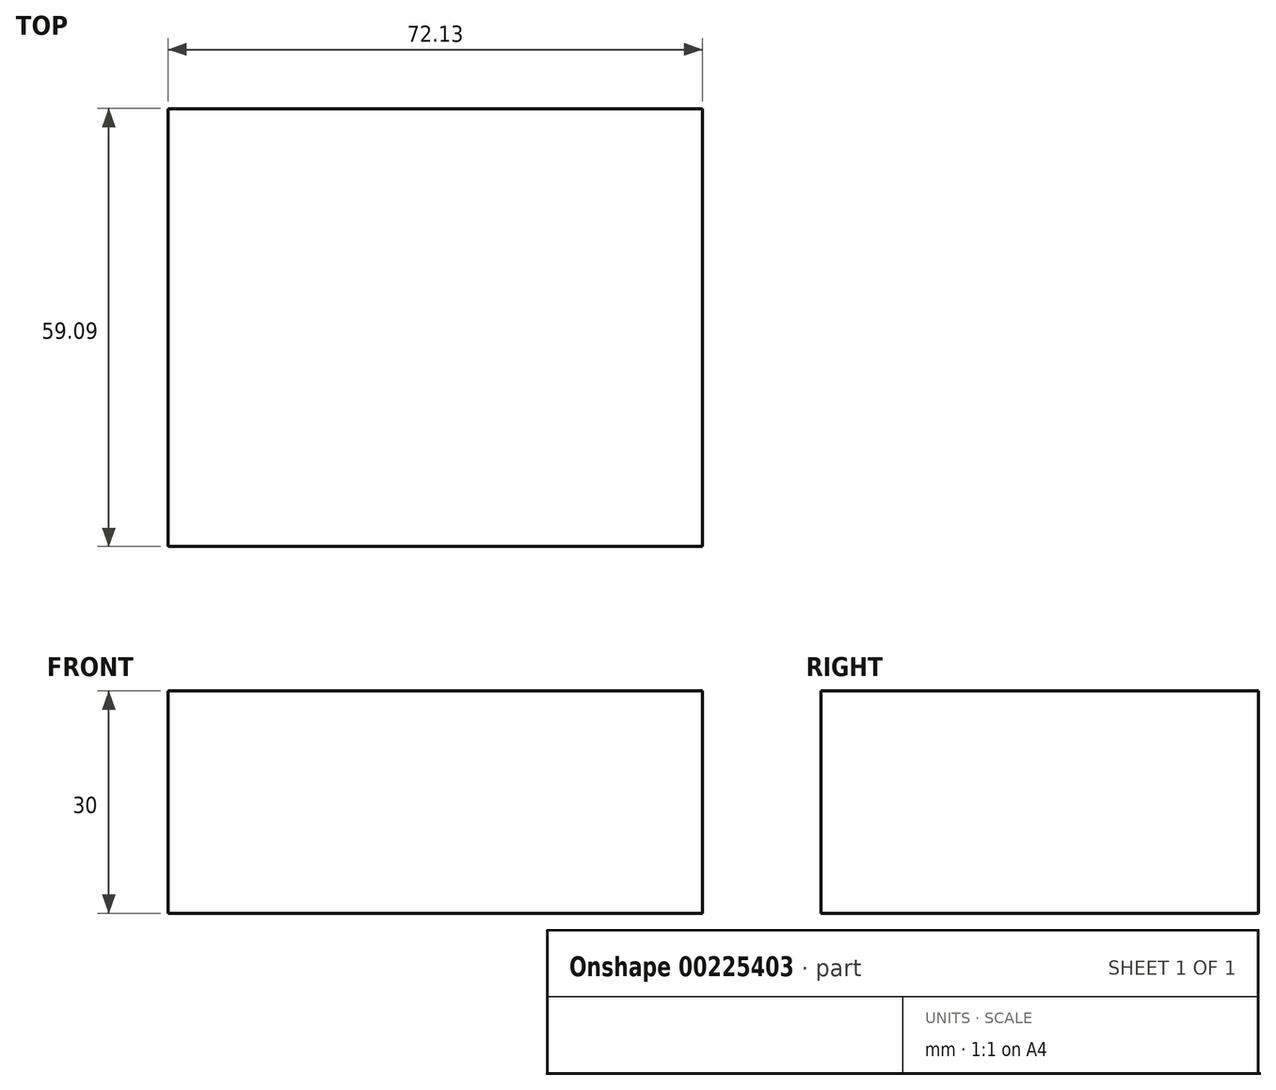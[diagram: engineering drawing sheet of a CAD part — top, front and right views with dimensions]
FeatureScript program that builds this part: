
annotation { "Feature Type Name" : "Feature", "Feature Type Description" : "" }
export const myFeature = defineFeature(function(context is Context, id is Id, definition is map)
    precondition{}
    {
        {
            var Q0;
            Q0=qCreatedBy(makeId("Top.planeOp"),FACE);
            var sketch = newSketch(context, id + "F0", { "sketchPlane" : qUnion([Q0])});
            skLineSegment(sketch, "E0.bottom", {"start": v(-26.84, 26.19) * mm, "end": v(45.3, 26.19) * mm});
            skLineSegment(sketch, "E0.top", {"start": v(-26.84, -32.9) * mm, "end": v(45.3, -32.9) * mm});
            skLineSegment(sketch, "E0.left", {"start": v(-26.84, 26.19) * mm, "end": v(-26.84, -32.9) * mm});
            skLineSegment(sketch, "E0.right", {"start": v(45.3, 26.19) * mm, "end": v(45.3, -32.9) * mm});
            skSolve(sketch);
        }
        {
            var Q0;
            Q0=makeQuery(id+"F0.imprint","IMPRINT",FACE,{"disambiguationData":[TD([[makeQuery(id+"F0.imprint","IMPRINT",EDGE,{"derivedFrom":sQuery(id+"F0.wireOp",EDGE,"E0.bottom")}),-1.0]])]});
            extrude(context, id + "F1", {"entities" : qUnion([Q0]), "depth" : 30 * mm});
        }
    });
